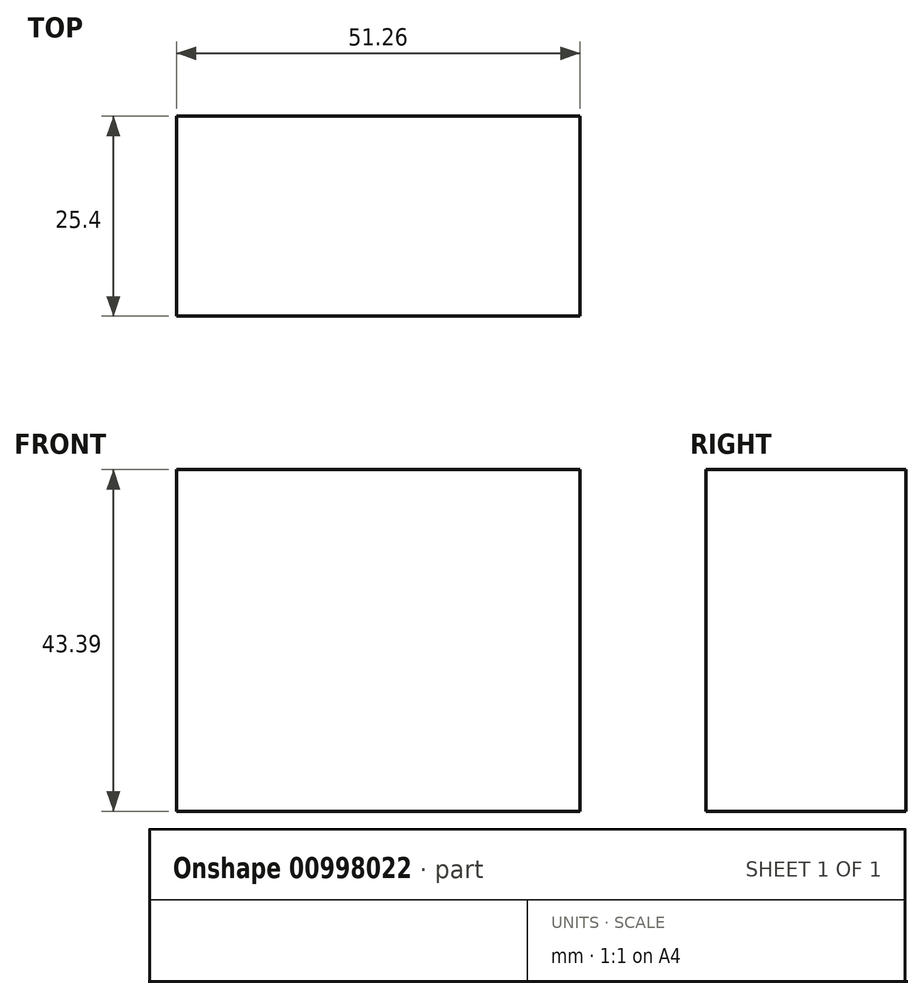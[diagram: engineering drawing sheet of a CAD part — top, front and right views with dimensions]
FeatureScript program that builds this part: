
annotation { "Feature Type Name" : "Feature", "Feature Type Description" : "" }
export const myFeature = defineFeature(function(context is Context, id is Id, definition is map)
    precondition{}
    {
        {
            var Q0;
            Q0=qCreatedBy(makeId("Front.planeOp"),FACE);
            var sketch = newSketch(context, id + "F0", { "sketchPlane" : qUnion([Q0])});
            skLineSegment(sketch, "E0.bottom", {"start": v(-51.26, 65.9) * mm, "end": v(0, 65.9) * mm});
            skLineSegment(sketch, "E0.top", {"start": v(-51.26, 22.51) * mm, "end": v(0, 22.51) * mm});
            skLineSegment(sketch, "E0.left", {"start": v(-51.26, 65.9) * mm, "end": v(-51.26, 22.51) * mm});
            skLineSegment(sketch, "E0.right", {"start": v(0, 65.9) * mm, "end": v(0, 22.51) * mm});
            skSolve(sketch);
        }
        {
            var Q0;
            Q0 = qSketchRegion(id + "F0", true);
            extrude(context, id + "F1", {"entities" : qUnion([Q0]), "depth" : 25.4 * mm, "offsetDistance" : 25.4 * mm});
        }
    });
